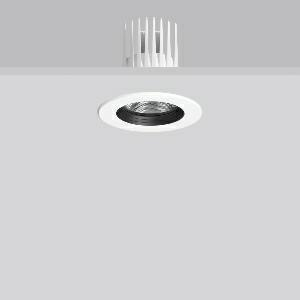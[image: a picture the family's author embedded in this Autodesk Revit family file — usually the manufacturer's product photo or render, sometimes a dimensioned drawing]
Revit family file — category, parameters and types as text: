
# Revit family: heledon_mini_e_901750_002_3_4789
name_source: partatom
category: Lighting Fixtures
units: mm (PartAtom-declared; Revit-internal decimal feet)

## family parameters
Cut with Voids When Loaded = No
Host = Face
Light Source = No
Part Type = Normal
Room Calculation Point = No
Round Connector Dimension = Use Diameter
Shared = No

## types (1)
- HELEDON mini E (1 x LED Modul 935, 3800 lm, 3500)
    Apparent Load = 29 VA
    Approval mark = CE
    CIE Flux Codes = 95 99 100 100 100
    Color Rendering = 92
    Color Temperature = 3500
    Default Elevation = 1800 mm
    Description = Series: HELEDON mini
Round recessed downlight. Housing: die-cast aluminium, powder-coated. Black plastic ring and recessed LED to prevent glare from the side. Optical assembly with reflector made of MIRO-Silver with 98% total light reflection for outstanding efficiency - can be changed without tools. Best colour rendering index Ra>90. Suitable for Recessed ceiling mounting. Installation without tools thanks to spring fastening system. Including separate LED converter with connecting cable 600 mm.High quality converter without flickering and stroboscopic effect. Through-wiring box (5 pole) available as accessory. The following accessories can be mounted without use of tools: interchangeable lenses, decorative glasses, honeycomb louvre, clear and frosted diffusers, white interchangeable plastic ring. 
Colour: traffic white, matt (RAL 9016)
Diameter: 124 mm
Height: 3 mm
Cut-out diameter: 114 mm
Recess height: 170 mm
Luminaire: recess height: 120 mm
Lamp: LED
Socket: without socket
Colour temperature: 3500K
Colour rendering index (CRI): 92
System power: 29 W
Rated luminous flux: 3800 lm
Luminous efficiency: 131 lm/W
Control gear: Regulated power supply
Protection class: II
Type of protection: IP 20
    Height = 0 mm  [stored 0 ft]
    Lamp = 1 x LED Modul 935
    Lamp Light Flux = 3800 lm
    Lamp count = 1
    Length = 124 mm  [stored 0.406824 ft]
    Lifetime = 50000 h
    Luminous efficacy = 131 lm/W
    Manufacturer = RZB
    ModVariant = No
    Model = 901750.002.3
    Mounting Place = Ceiling
    Mounting Type = Recessed
    Number of Poles = 1
    OnlyDefault = Yes
    Power Factor = 1
    Product Name = HELEDON mini E
    Product group = Recessed downlights
    ProductGroupID = 402
    Protection Class = Protection class II
    Protection Degree = IP 20
    RLX_Detail_Level = 1
    RLX_Emergency_Light_Flux = 0 lm
    RLX_Emergency_Type = 0
    RLX_Emergency_Type_DB = No
    RlxData = <blob elided: 125773 chars, md5=54389ab7>
    Socket = socket
    Standby Power = 0 W
    System Light Flux = 3800 lm
    System Power = 29 W
    Type Comments = Product without accessories
    Type Image = 901657.002.jpg
    URL = http://relux.com
    VarID = ---
    Voltage = 230 V
    Voltage Range = 220-240 V
    Weight = 0.00 kg
    Width = 0 mm  [stored 0 ft]

note: [stored X ft] marks values corroborated as IEEE doubles in the binary element streams (Revit-internal decimal feet)

## geometry (parser evidence)
native form markers: Blend x4, Sweep x11
no freeform markers — native parametric forms only
